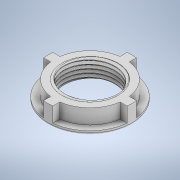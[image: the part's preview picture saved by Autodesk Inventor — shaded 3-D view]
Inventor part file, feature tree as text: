
AUTODESK INVENTOR PART (.ipt)
format: ipt  version: 2020.2 (Build 242310000, 310)  size: 706,048 bytes
history: native  units: mm
features: sketch x4, extrude x2, fillet x1, thread x1, revolve x1, helix x1
ambient origin geometry x8: Origin, YZ Plane, XZ Plane, XY Plane, X Axis, Y Axis, Z Axis, Center Point
bodies: Solid1 (feature_tree), Solid8 (feature_tree)
feature tree (10):
  extrude  "Washer"  Depth=30.0mm
  extrude  "Nut"  Depth=8.0mm TaperAngle=0.0deg
  fillet  "Fillet1"  Radius=5.0mm
  thread  "Thread8"  [1 undecoded]
  revolve  "Revolution7"  [1 undecoded]
  helix  "Coil7"  [1 undecoded]
  sketch  "Sketch1"  dims[d0=45.0mm d1=30.0mm]
  sketch  "Sketch2"  dims[d2=2.0mm d3=0.0mm d5=8.0mm d6=0.0mm d9=5.0mm d10=40.0mm d12=360.0deg]
  sketch  "Sketch15"  dims[d23=9.599311mm d43=9.599311mm d63=9.599311mm]
  sketch  "Sketch16"  dims[d83=9.599311mm d104=9.599311mm d115=37.5mm d125=9.599311mm d136=1.0mm d137=10.0mm d138=0.0mm d139=9.599311mm d140=0.320166mm d141=0.320166mm d144=2.0mm d146=9.599311mm d148=0.0mm d149=2.002mm d150=14.0mm d151=10.0mm d152=0.0mm d153=0.0mm d154=0.0mm d155=0.0mm d156=0.0mm]
note: 3 required parameter values undecoded (feature->parameter linkage not recoverable at this tier; creation-order binding heuristic only, values carry confidence <= 0.55)